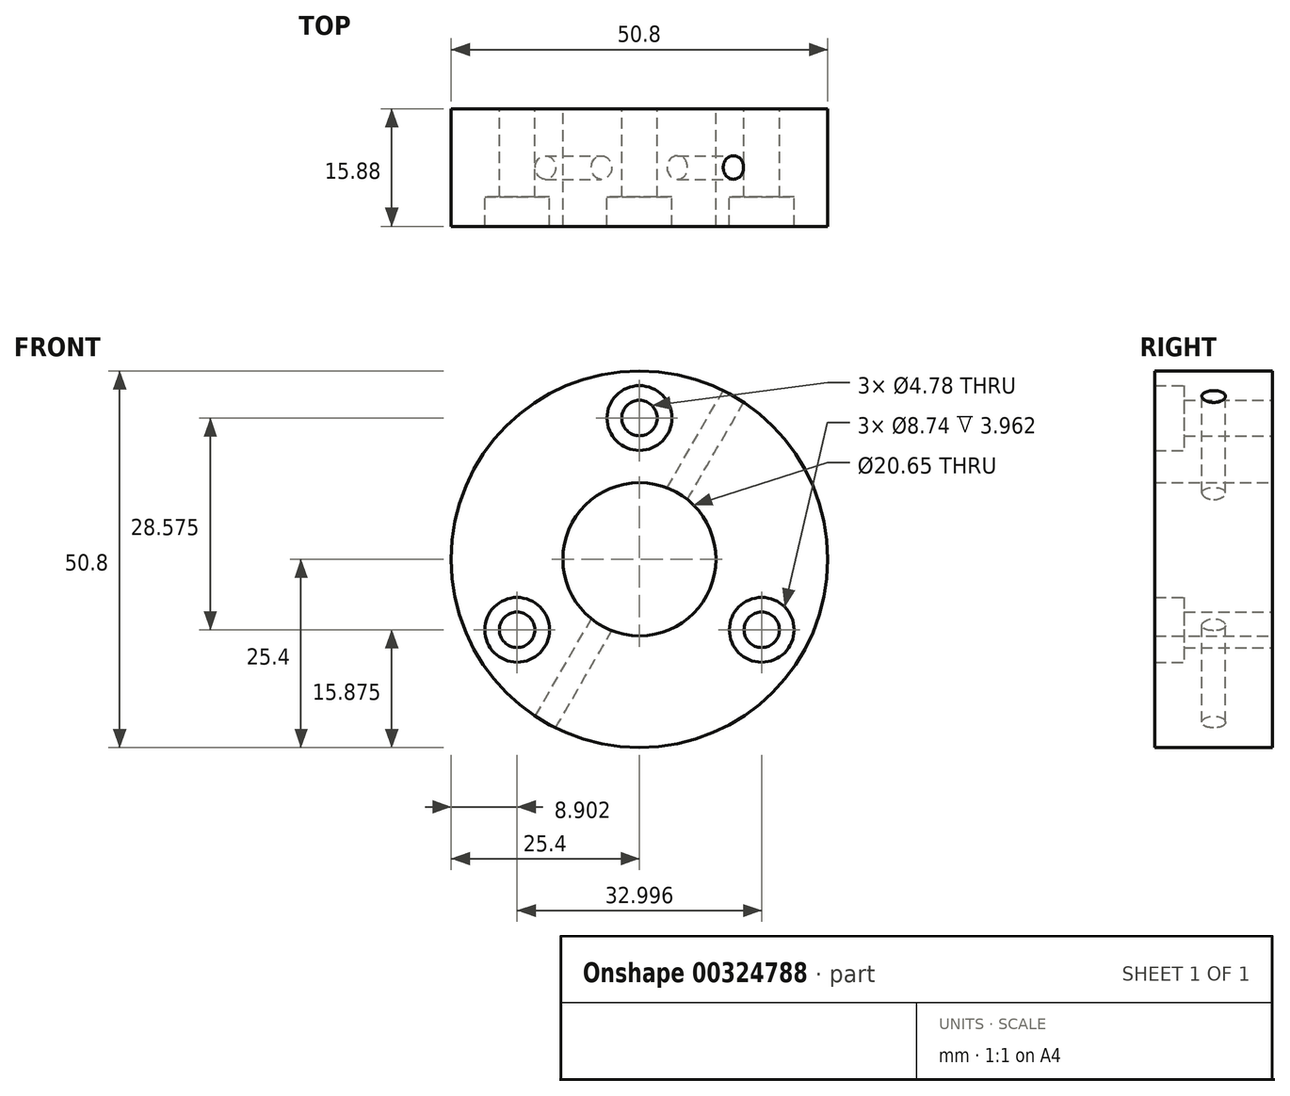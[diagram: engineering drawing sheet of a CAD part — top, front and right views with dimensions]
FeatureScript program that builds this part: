
annotation { "Feature Type Name" : "Feature", "Feature Type Description" : "" }
export const myFeature = defineFeature(function(context is Context, id is Id, definition is map)
    precondition{}
    {
        {
            var Q0;
            Q0=qCreatedBy(makeId("Front.planeOp"),FACE);
            var sketch = newSketch(context, id + "F0", { "sketchPlane" : qUnion([Q0])});
            skCircle(sketch, "E0", {"center": v(0, 0) * mm, "radius": 25.4 * mm});
            skCircle(sketch, "E1", {"center": v(0, 0) * mm, "radius": 10.33 * mm});
            skSolve(sketch);
        }
        {
            var Q0;
            Q0=makeQuery(id+"F0.imprint","IMPRINT",FACE,{"disambiguationData":[TD([[makeQuery(id+"F0.imprint","IMPRINT",EDGE,{"derivedFrom":sQuery(id+"F0.wireOp",EDGE,"E0")}),1.0]])]});
            extrude(context, id + "F1", {"entities" : qUnion([Q0]), "depth" : 15.88 * mm, "offsetDistance" : 25.4 * mm});
        }
        {
            var Q0;
            Q0=makeQuery(id+"F1.opExtrude","CAP_FACE",FACE,{"disambiguationData":[OSD([sQuery(id+"F0.wireOp",EDGE,"E0"),sQuery(id+"F0.wireOp",EDGE,"E1")])],"isStart":false});
            var sketch = newSketch(context, id + "F2", { "sketchPlane" : qUnion([Q0])});
            skPoint(sketch, "E2", {"position": v(0, 19.05) * mm});
            skPoint(sketch, "E3.1.0", {"position": v(-16.5, -9.52) * mm});
            skPoint(sketch, "E3.2.0", {"position": v(16.5, -9.53) * mm});
            skPoint(sketch, "E3.center", {"position": v(0, 0) * mm});
            skSolve(sketch);
        }
        {
            var Q0;
            Q0=sQuery(id+"F2.wireOp",VERTEX,"E2");
            var Q1;
            Q1=sQuery(id+"F2.wireOp",VERTEX,"E3.1.0");
            var Q2;
            Q2=sQuery(id+"F2.wireOp",VERTEX,"E3.2.0");
            var Q3;
            Q3=makeQuery(id+"F1.opExtrude","SWEPT_BODY",BODY,{"disambiguationData":[OSD([sQuery(id+"F0.wireOp",EDGE,"E0"),sQuery(id+"F0.wireOp",EDGE,"E1")])]});
            hole(context, id + "F3", {"style" : HoleStyle.C_BORE, "endStyle" : HoleEndStyle.THROUGH, "holeDiameter" : 4.78 * mm, "cBoreDiameter" : 8.74 * mm, "cBoreDepth" : 3.96 * mm, "majorDiameter" : 6.35 * mm, "tappedDepth" : 12.7 * mm, "tapClearance" : 3, "locations" : qUnion([Q0, Q1, Q2]), "scope" : qUnion([Q3])});
        }
        {
            var Q0;
            Q0=makeQuery(id+"F1.opExtrude","CAP_EDGE",EDGE,{"disambiguationData":[OSD([sQuery(id+"F0.wireOp",EDGE,"E1")])],"isStart":false});
            var Q1;
            Q1=qCreatedBy(makeId("Right.planeOp"),FACE);
            cPlane(context, id + "F4", {"entities" : qUnion([Q0, Q1]), "cplaneType" : CPlaneType.LINE_ANGLE, "offset" : 25.4 * mm, "angle" : 60 * degree, "width" : 152.4 * mm, "height" : 152.4 * mm});
        }
        {
            var Q0;
            Q0=qCreatedBy(id+"F4.planeOp",FACE);
            cPlane(context, id + "F5", {"entities" : qUnion([Q0]), "cplaneType" : CPlaneType.OFFSET, "offset" : 25.4 * mm, "oppositeDirection" : true, "width" : 152.4 * mm, "height" : 152.4 * mm});
        }
        {
            var Q0;
            Q0=qCreatedBy(id+"F5.planeOp",FACE);
            var sketch = newSketch(context, id + "F6", { "sketchPlane" : qUnion([Q0])});
            skCircle(sketch, "E4", {"center": v(0.82, 7.95) * mm, "radius": 1.59 * mm});
            skSolve(sketch);
        }
        {
            var Q0;
            Q0=makeQuery(id+"F6.imprint","IMPRINT",FACE,{"disambiguationData":[TD([[makeQuery(id+"F6.imprint","IMPRINT",EDGE,{"derivedFrom":sQuery(id+"F6.wireOp",EDGE,"E4")}),1.0]])]});
            extrude(context, id + "F7", {"entities" : qUnion([Q0]), "operationType" : NewBodyOperationType.REMOVE, "endBound" : BoundingType.THROUGH_ALL, "oppositeDirection" : true, "depth" : 25.4 * mm, "offsetDistance" : 25.4 * mm});
        }
        {
            var Q0;
            Q0=qCreatedBy(id+"F5.planeOp",FACE);
            var sketch = newSketch(context, id + "F8", { "sketchPlane" : qUnion([Q0])});
            skCircle(sketch, "E5", {"center": v(0, 7.92) * mm, "radius": 1.59 * mm});
            skSolve(sketch);
        }
        {
            var Q0;
            Q0=makeQuery(id+"F8.imprint","IMPRINT",FACE,{"disambiguationData":[TD([[makeQuery(id+"F8.imprint","IMPRINT",EDGE,{"derivedFrom":sQuery(id+"F8.wireOp",EDGE,"E5")}),1.0]])]});
            extrude(context, id + "F9", {"entities" : qUnion([Q0]), "operationType" : NewBodyOperationType.REMOVE, "endBound" : BoundingType.THROUGH_ALL, "depth" : 25.4 * mm, "offsetDistance" : 25.4 * mm});
        }
    });
